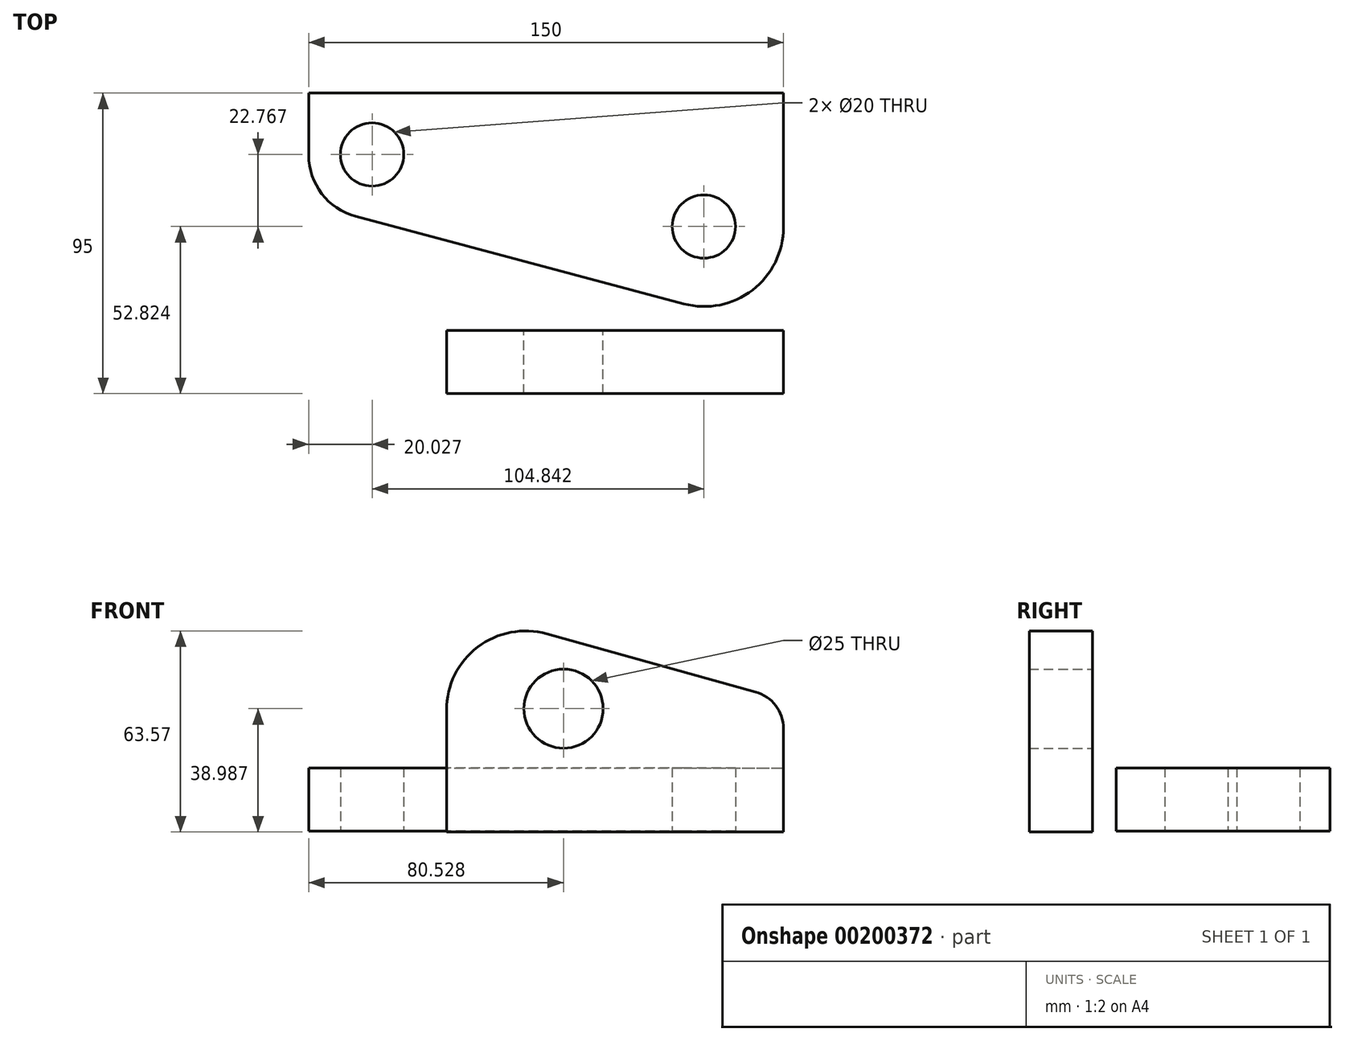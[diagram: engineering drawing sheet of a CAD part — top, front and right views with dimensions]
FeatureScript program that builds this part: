
annotation { "Feature Type Name" : "Feature", "Feature Type Description" : "" }
export const myFeature = defineFeature(function(context is Context, id is Id, definition is map)
    precondition{}
    {
        {
            var Q0;
            Q0=qCreatedBy(makeId("Top.planeOp"),FACE);
            var sketch = newSketch(context, id + "F0", { "sketchPlane" : qUnion([Q0])});
            skLineSegment(sketch, "E0", {"start": v(-150, 75) * mm, "end": v(0, 75) * mm});
            skLineSegment(sketch, "E1", {"start": v(0, 75) * mm, "end": v(0, 32.54) * mm});
            skLineSegment(sketch, "E2", {"start": v(-31.44, 8.38) * mm, "end": v(-135.15, 36.04) * mm});
            skLineSegment(sketch, "E3", {"start": v(-150, 55.37) * mm, "end": v(-150, 75) * mm});
            skPoint(sketch, "E4.visualSharp", {"position": v(0, 0) * mm});
            skArc(sketch, "E4.filletArc", {"start": v(-31.44, 8.38) * mm, "mid": v(-9.77, 12.72) * mm, "end": v(0, 32.54) * mm});
            skPoint(sketch, "E5.visualSharp", {"position": v(-150, 40) * mm});
            skArc(sketch, "E5.filletArc", {"start": v(-150, 55.37) * mm, "mid": v(-145.86, 43.18) * mm, "end": v(-135.15, 36.04) * mm});
            skCircle(sketch, "E6", {"center": v(-129.97, 55.6) * mm, "radius": 10 * mm});
            skCircle(sketch, "E7", {"center": v(-25.13, 32.82) * mm, "radius": 10 * mm});
            skSolve(sketch);
        }
        {
            var Q0;
            Q0 = qSketchRegion(id + "F0", true);
            extrude(context, id + "F1", {"entities" : qUnion([Q0]), "depth" : 20 * mm});
        }
        {
            var Q0;
            Q0=qCreatedBy(makeId("Front.planeOp"),FACE);
            var sketch = newSketch(context, id + "F2", { "sketchPlane" : qUnion([Q0])});
            skLineSegment(sketch, "E8", {"start": v(0, -0.26) * mm, "end": v(-106.46, -0.26) * mm});
            skLineSegment(sketch, "E9", {"start": v(-106.46, -0.26) * mm, "end": v(-106.46, 38.3) * mm});
            skLineSegment(sketch, "E10", {"start": v(-74.75, 62.39) * mm, "end": v(-8.78, 44) * mm});
            skLineSegment(sketch, "E11", {"start": v(0, 32.45) * mm, "end": v(0, -0.26) * mm});
            skPoint(sketch, "E12.visualSharp", {"position": v(0, 41.56) * mm});
            skArc(sketch, "E12.filletArc", {"start": v(0, 32.45) * mm, "mid": v(-2.44, 39.7) * mm, "end": v(-8.78, 44) * mm});
            skPoint(sketch, "E13.visualSharp", {"position": v(-106.46, 71.23) * mm});
            skArc(sketch, "E13.filletArc", {"start": v(-74.75, 62.39) * mm, "mid": v(-96.58, 58.22) * mm, "end": v(-106.46, 38.3) * mm});
            skCircle(sketch, "E14", {"center": v(-69.47, 38.73) * mm, "radius": 12.5 * mm});
            skSolve(sketch);
        }
        {
            var Q0;
            Q0 = qSketchRegion(id + "F2", true);
            extrude(context, id + "F3", {"entities" : qUnion([Q0]), "depth" : 20 * mm});
        }
    });
